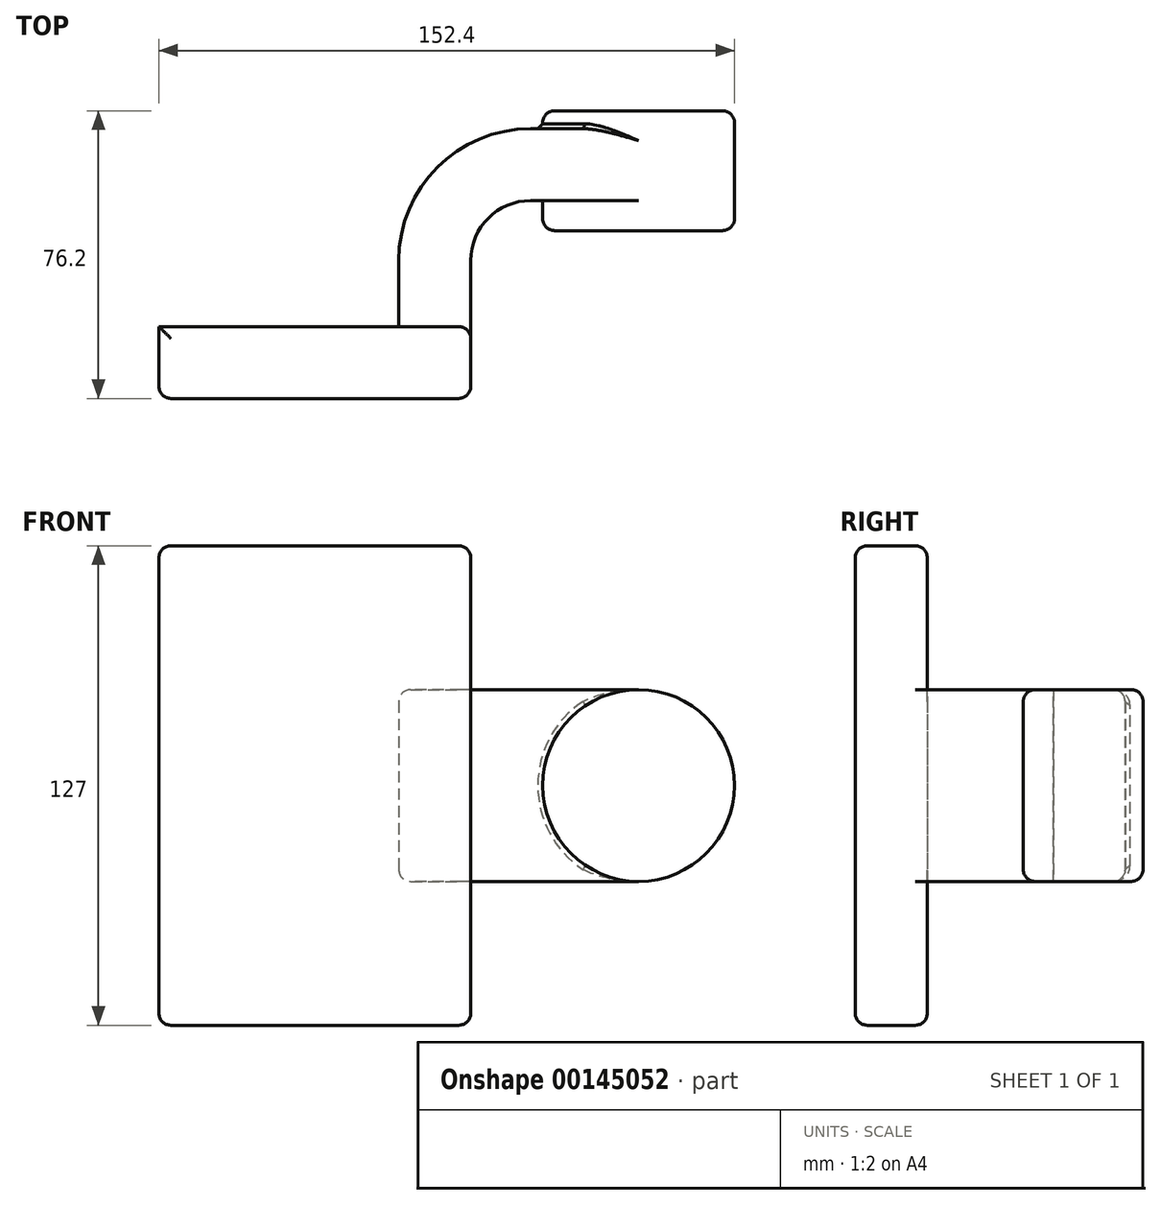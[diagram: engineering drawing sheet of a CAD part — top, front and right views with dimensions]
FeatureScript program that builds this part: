
annotation { "Feature Type Name" : "Feature", "Feature Type Description" : "" }
export const myFeature = defineFeature(function(context is Context, id is Id, definition is map)
    precondition{}
    {
        {
            var Q0;
            Q0=qCreatedBy(makeId("Top.planeOp"),FACE);
            var sketch = newSketch(context, id + "F0", { "sketchPlane" : qUnion([Q0])});
            skLineSegment(sketch, "E0.bottom", {"start": v(4.1, 0.88) * mm, "end": v(86.64, 0.88) * mm});
            skLineSegment(sketch, "E0.top", {"start": v(4.1, 19.93) * mm, "end": v(86.64, 19.93) * mm});
            skLineSegment(sketch, "E0.left", {"start": v(4.1, 0.88) * mm, "end": v(4.1, 19.93) * mm});
            skLineSegment(sketch, "E0.right", {"start": v(86.64, 0.88) * mm, "end": v(86.64, 19.93) * mm});
            skLineSegment(sketch, "E1.bottom", {"start": v(105.7, 45.33) * mm, "end": v(156.5, 45.33) * mm});
            skLineSegment(sketch, "E1.top", {"start": v(105.7, 77.08) * mm, "end": v(156.5, 77.08) * mm});
            skLineSegment(sketch, "E1.left", {"start": v(105.7, 45.33) * mm, "end": v(105.7, 77.08) * mm});
            skLineSegment(sketch, "E1.right", {"start": v(156.5, 45.33) * mm, "end": v(156.5, 77.08) * mm});
            skLineSegment(sketch, "E2", {"start": v(86.64, 19.93) * mm, "end": v(86.64, 37.4) * mm});
            skArc(sketch, "E3", {"start": v(86.64, 37.4) * mm, "mid": v(91.3, 48.63) * mm, "end": v(102.52, 53.28) * mm});
            skLineSegment(sketch, "E4", {"start": v(102.52, 53.28) * mm, "end": v(131.1, 53.28) * mm});
            skLineSegment(sketch, "E5.0", {"start": v(102.52, 72.33) * mm, "end": v(131.1, 72.33) * mm});
            skArc(sketch, "E5.1", {"start": v(67.6, 37.4) * mm, "mid": v(77.82, 62.1) * mm, "end": v(102.52, 72.33) * mm});
            skLineSegment(sketch, "E5.2", {"start": v(67.6, 19.93) * mm, "end": v(67.6, 37.4) * mm});
            skLineSegment(sketch, "E6", {"start": v(131.1, 45.33) * mm, "end": v(131.1, 77.08) * mm});
            skFitSpline(sketch, "E7", {"points": [v(4.1, 19.93) * mm, v(102.52, 72.33) * mm], "startDerivative": vector(0, 39) * mm, "endDerivative": vector(273.47, 0) * mm});
            skSolve(sketch);
        }
        {
            var Q0;
            Q0=makeQuery(id+"F0.imprint","IMPRINT",FACE,{"disambiguationData":[TD([[makeQuery(id+"F0.imprint","IMPRINT",EDGE,{"derivedFrom":sQuery(id+"F0.wireOp",EDGE,"E0.bottom")}),1.0]])]});
            extrude(context, id + "F1", {"entities" : qUnion([Q0]), "endBound" : BoundingType.SYMMETRIC, "depth" : 127 * mm});
        }
        {
            var Q0;
            {var subQ1=sQuery(id+"F0.wireOp",EDGE,"E2");Q0=makeQuery(id+"F0.imprint","IMPRINT",FACE,{"disambiguationData":[TD([[makeQuery(id+"F0.imprint","IMPRINT",EDGE,{"derivedFrom":subQ1}),1.0]])]});}
            var Q1;
            {var subQ0=sQuery(id+"F0.wireOp",EDGE,"E4");var subQ1=sQuery(id+"F0.wireOp",EDGE,"E1.left");var subQ2=makeQuery(id+"F0.imprint","INTERSECT",VERTEX,{"derivedFrom":[subQ1,subQ0]});Q1=makeQuery(id+"F0.imprint","IMPRINT",FACE,{"disambiguationData":[TD([[makeQuery(id+"F0.imprint","IMPRINT",EDGE,{"disambiguationData":[TD([[subQ2,-1.0]])],"derivedFrom":subQ1}),-1.0]])]});}
            extrude(context, id + "F2", {"entities" : qUnion([Q0, Q1]), "operationType" : NewBodyOperationType.ADD, "endBound" : BoundingType.SYMMETRIC, "depth" : 50.8 * mm});
        }
        {
            var Q0;
            Q0=makeQuery(id+"F0.imprint","IMPRINT",FACE,{"disambiguationData":[TD([[makeQuery(id+"F0.imprint","IMPRINT",EDGE,{"derivedFrom":sQuery(id+"F0.wireOp",EDGE,"E5.1")}),1.0]])]});
            extrude(context, id + "F3", {"entities" : qUnion([Q0]), "operationType" : NewBodyOperationType.ADD, "endBound" : BoundingType.SYMMETRIC, "depth" : 25.4 * mm});
        }
        {
            var Q0;
            {var subQ0=sQuery(id+"F0.wireOp",EDGE,"E1.right");Q0=makeQuery(id+"F0.imprint","IMPRINT",FACE,{"disambiguationData":[TD([[makeQuery(id+"F0.imprint","IMPRINT",EDGE,{"derivedFrom":subQ0}),1.0]])]});}
            var Q1;
            Q1=sQuery(id+"F0.wireOp",EDGE,"E6");
            revolve(context, id + "F4", {"operationType" : NewBodyOperationType.ADD, "entities" : qUnion([Q0]), "axis" : qUnion([Q1]), "revolveType" : RevolveType.FULL});
        }
        {
            var Q0;
            Q0=makeQuery(id+"F4.opRevolve","SWEPT_FACE",FACE,{"disambiguationData":[OSD([sQuery(id+"F0.wireOp",EDGE,"E1.top")])]});
            var Q1;
            Q1=makeQuery(id+"F4.opRevolve","SWEPT_FACE",FACE,{"disambiguationData":[OSD([sQuery(id+"F0.wireOp",EDGE,"E1.bottom")])]});
            var Q2;
            Q2=makeQuery(id+"F2.opExtrude","CAP_EDGE",EDGE,{"disambiguationData":[OSD([sQuery(id+"F0.wireOp",EDGE,"E5.1")])],"isStart":false});
            var Q3;
            Q3=makeQuery(id+"F2.opExtrude","CAP_EDGE",EDGE,{"disambiguationData":[OSD([sQuery(id+"F0.wireOp",EDGE,"E5.1")])],"isStart":true});
            var Q4;
            Q4=makeQuery(id+"F3.opExtrude","CAP_EDGE",EDGE,{"disambiguationData":[OSD([sQuery(id+"F0.wireOp",EDGE,"E0.top")])],"isStart":true});
            var Q5;
            Q5=makeQuery(id+"F3.opExtrude","CAP_EDGE",EDGE,{"disambiguationData":[OSD([sQuery(id+"F0.wireOp",EDGE,"E5.1")])],"isStart":true});
            var Q6;
            Q6=makeQuery(id+"F3.opExtrude","CAP_EDGE",EDGE,{"disambiguationData":[OSD([sQuery(id+"F0.wireOp",EDGE,"E5.1")])],"isStart":false});
            var Q7;
            Q7=makeQuery(id+"F3.opExtrude","CAP_EDGE",EDGE,{"disambiguationData":[OSD([sQuery(id+"F0.wireOp",EDGE,"E0.top")])],"isStart":false});
            var Q8;
            Q8=makeQuery(id+"F2.opExtrude","CAP_EDGE",EDGE,{"disambiguationData":[OSD([sQuery(id+"F0.wireOp",EDGE,"E0.top")])],"isStart":false});
            var Q9;
            {var subQ0=sQuery(id+"F0.wireOp",EDGE,"E0.top");var subQ1=sQuery(id+"F0.wireOp",EDGE,"E5.2");var subQ2=sQuery(id+"F0.wireOp",EDGE,"E5.1");Q9=makeQuery(id+"F3.boolean.opBoolean","SPLIT",EDGE,{"disambiguationData":[TD([makeQuery(id+"F3.opExtrude","CAP_FACE",FACE,{"disambiguationData":[OSD([subQ0,subQ2,subQ1,sQuery(id+"F0.wireOp",EDGE,"E7")])],"isStart":false})])],"derivedFrom":makeQuery(id+"F2.opExtrude","SWEPT_EDGE",EDGE,{"disambiguationData":[OSD([subQ0,subQ1])]})});}
            var Q10;
            {var subQ0=sQuery(id+"F0.wireOp",EDGE,"E0.top");var subQ1=sQuery(id+"F0.wireOp",EDGE,"E5.2");var subQ2=sQuery(id+"F0.wireOp",EDGE,"E5.1");Q10=makeQuery(id+"F3.boolean.opBoolean","SPLIT",EDGE,{"disambiguationData":[TD([makeQuery(id+"F3.opExtrude","CAP_FACE",FACE,{"disambiguationData":[OSD([subQ0,subQ2,subQ1,sQuery(id+"F0.wireOp",EDGE,"E7")])],"isStart":true})])],"derivedFrom":makeQuery(id+"F2.opExtrude","SWEPT_EDGE",EDGE,{"disambiguationData":[OSD([subQ0,subQ1])]})});}
            var Q11;
            Q11=makeQuery(id+"F1.opExtrude","CAP_EDGE",EDGE,{"disambiguationData":[OSD([sQuery(id+"F0.wireOp",EDGE,"E0.left")])],"isStart":true});
            var Q12;
            Q12=makeQuery(id+"F1.opExtrude","CAP_EDGE",EDGE,{"disambiguationData":[OSD([sQuery(id+"F0.wireOp",EDGE,"E0.left")])],"isStart":false});
            var Q13;
            Q13=makeQuery(id+"F1.opExtrude","CAP_EDGE",EDGE,{"disambiguationData":[OSD([sQuery(id+"F0.wireOp",EDGE,"E0.top")])],"isStart":false});
            var Q14;
            Q14=makeQuery(id+"F1.opExtrude","CAP_EDGE",EDGE,{"disambiguationData":[OSD([sQuery(id+"F0.wireOp",EDGE,"E0.right")])],"isStart":false});
            var Q15;
            {var subQ0=sQuery(id+"F0.wireOp",EDGE,"E2");var subQ1=sQuery(id+"F0.wireOp",EDGE,"E0.top");var subQ2=sQuery(id+"F0.wireOp",EDGE,"E0.right");Q15=makeQuery(id+"F2.boolean.opBoolean","SPLIT",EDGE,{"disambiguationData":[TD([makeQuery(id+"F1.opExtrude","CAP_FACE",FACE,{"disambiguationData":[OSD([sQuery(id+"F0.wireOp",EDGE,"E0.bottom"),subQ1,sQuery(id+"F0.wireOp",EDGE,"E0.left"),subQ2])],"isStart":false})])],"derivedFrom":makeQuery(id+"F1.opExtrude","SWEPT_EDGE",EDGE,{"disambiguationData":[OSD([subQ1,subQ2,subQ0])]})});}
            var Q16;
            {var subQ0=sQuery(id+"F0.wireOp",EDGE,"E2");var subQ1=sQuery(id+"F0.wireOp",EDGE,"E0.top");var subQ2=sQuery(id+"F0.wireOp",EDGE,"E0.right");Q16=makeQuery(id+"F2.boolean.opBoolean","SPLIT",EDGE,{"disambiguationData":[TD([makeQuery(id+"F1.opExtrude","CAP_FACE",FACE,{"disambiguationData":[OSD([sQuery(id+"F0.wireOp",EDGE,"E0.bottom"),subQ1,sQuery(id+"F0.wireOp",EDGE,"E0.left"),subQ2])],"isStart":true})])],"derivedFrom":makeQuery(id+"F1.opExtrude","SWEPT_EDGE",EDGE,{"disambiguationData":[OSD([subQ1,subQ2,subQ0])]})});}
            var Q17;
            Q17=makeQuery(id+"F1.opExtrude","CAP_EDGE",EDGE,{"disambiguationData":[OSD([sQuery(id+"F0.wireOp",EDGE,"E0.right")])],"isStart":true});
            var Q18;
            Q18=makeQuery(id+"F1.opExtrude","CAP_EDGE",EDGE,{"disambiguationData":[OSD([sQuery(id+"F0.wireOp",EDGE,"E0.top")])],"isStart":true});
            var Q19;
            Q19=makeQuery(id+"F1.opExtrude","SWEPT_EDGE",EDGE,{"disambiguationData":[OSD([sQuery(id+"F0.wireOp",EDGE,"E0.bottom"),sQuery(id+"F0.wireOp",EDGE,"E0.left")])]});
            var Q20;
            Q20=makeQuery(id+"F1.opExtrude","CAP_EDGE",EDGE,{"disambiguationData":[OSD([sQuery(id+"F0.wireOp",EDGE,"E0.bottom")])],"isStart":true});
            var Q21;
            Q21=makeQuery(id+"F1.opExtrude","SWEPT_EDGE",EDGE,{"disambiguationData":[OSD([sQuery(id+"F0.wireOp",EDGE,"E0.bottom"),sQuery(id+"F0.wireOp",EDGE,"E0.right")])]});
            var Q22;
            Q22=makeQuery(id+"F1.opExtrude","CAP_EDGE",EDGE,{"disambiguationData":[OSD([sQuery(id+"F0.wireOp",EDGE,"E0.bottom")])],"isStart":false});
            fillet(context, id + "F5", {"entities" : qUnion([Q0, Q1, Q2, Q3, Q4, Q5, Q6, Q7, Q8, Q9, Q10, Q11, Q12, Q13, Q14, Q15, Q16, Q17, Q18, Q19, Q20, Q21, Q22]), "radius" : 3.17 * mm, "tangentPropagation" : true, "allowEdgeOverflow" : false});
        }
        {
            var Q0;
            Q0=makeQuery(id+"F3.opExtrude","CAP_EDGE",EDGE,{"disambiguationData":[OSD([sQuery(id+"F0.wireOp",EDGE,"E7")])],"isStart":true});
            var Q1;
            Q1=makeQuery(id+"F3.opExtrude","CAP_EDGE",EDGE,{"disambiguationData":[OSD([sQuery(id+"F0.wireOp",EDGE,"E7")])],"isStart":false});
            var Q2;
            Q2=makeQuery(id+"F4.boolean.opBoolean","INTERSECT",EDGE,{"derivedFrom":[makeQuery(id+"F2.opExtrude","SWEPT_FACE",FACE,{"disambiguationData":[OSD([sQuery(id+"F0.wireOp",EDGE,"E5.0")])]}),makeQuery(id+"F4.opRevolve","SWEPT_FACE",FACE,{"disambiguationData":[OSD([sQuery(id+"F0.wireOp",EDGE,"E1.right")])]})]});
            chamfer(context, id + "F6", {"entities" : qUnion([Q0, Q1, Q2]), "width" : 1.27 * mm, "tangentPropagation" : true});
        }
    });
